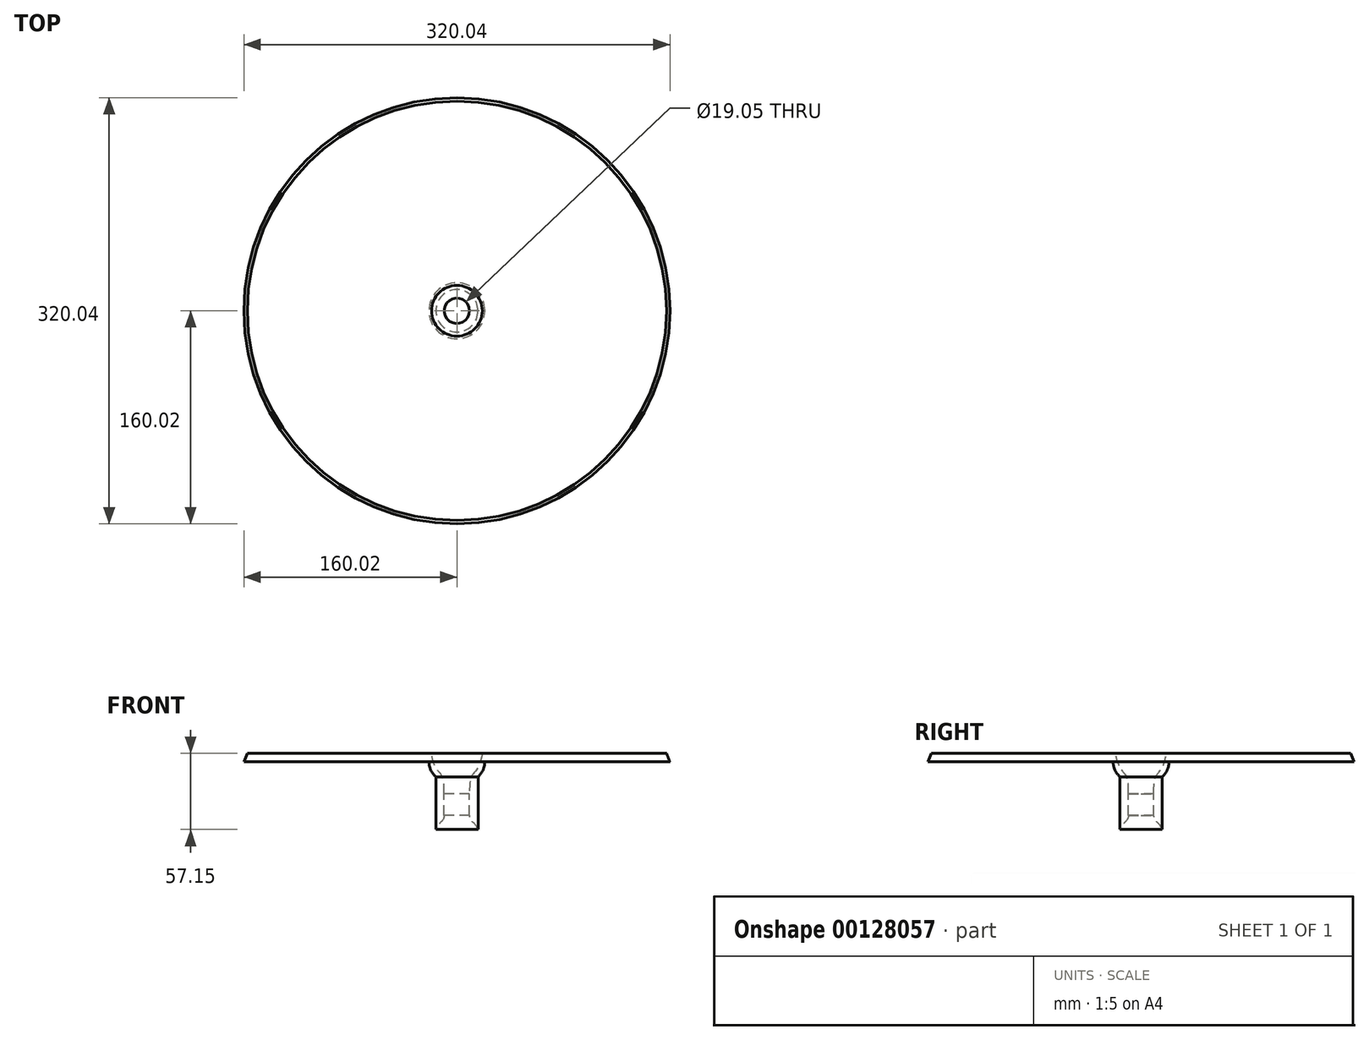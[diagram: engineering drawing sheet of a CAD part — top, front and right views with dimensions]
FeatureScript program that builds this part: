
annotation { "Feature Type Name" : "Feature", "Feature Type Description" : "" }
export const myFeature = defineFeature(function(context is Context, id is Id, definition is map)
    precondition{}
    {
        {
            var Q0;
            Q0=qCreatedBy(makeId("Front.planeOp"),FACE);
            var sketch = newSketch(context, id + "F0", { "sketchPlane" : qUnion([Q0])});
            skLineSegment(sketch, "E0", {"start": v(21, 0) * mm, "end": v(160.02, 0) * mm});
            skLineSegment(sketch, "E1", {"start": v(160.02, 0) * mm, "end": v(157.48, 6.35) * mm});
            skLineSegment(sketch, "E2", {"start": v(157.48, 6.35) * mm, "end": v(19.05, 6.35) * mm});
            skLineSegment(sketch, "E3", {"start": v(15.88, -11.25) * mm, "end": v(15.88, -50.8) * mm});
            skLineSegment(sketch, "E4", {"start": v(9.53, -40.06) * mm, "end": v(9.53, -23.9) * mm});
            skPoint(sketch, "E5.visualSharp", {"position": v(9.53, -23.9) * mm});
            skArc(sketch, "E6", {"start": v(15.88, -11.25) * mm, "mid": v(19.6, -6.15) * mm, "end": v(21, 0) * mm});
            skLineSegment(sketch, "E7", {"start": v(0, 59.49) * mm, "end": v(0, -54.68) * mm, "construction": true});
            skFitSpline(sketch, "E8", {"points": [v(19.05, 6.35) * mm, v(11.67, -9.78) * mm, v(9.53, -23.9) * mm], "startDerivative": vector(-10, -66.16) * mm, "endDerivative": vector(0.6, -46.18) * mm});
            skFitSpline(sketch, "E9", {"points": [v(15.88, -50.8) * mm, v(9.53, -40.06) * mm], "startDerivative": vector(-4.22, 14.92) * mm, "endDerivative": vector(0.17, 14.68) * mm});
            skSolve(sketch);
        }
        {
            var Q0;
            Q0=makeQuery(id+"F0.imprint","IMPRINT",FACE,{"disambiguationData":[TD([[makeQuery(id+"F0.imprint","IMPRINT",EDGE,{"derivedFrom":sQuery(id+"F0.wireOp",EDGE,"E0")}),1.0]])]});
            var Q1;
            Q1=sQuery(id+"F0.wireOp",EDGE,"E7");
            revolve(context, id + "F1", {"entities" : qUnion([Q0]), "axis" : qUnion([Q1]), "revolveType" : RevolveType.FULL});
        }
    });
